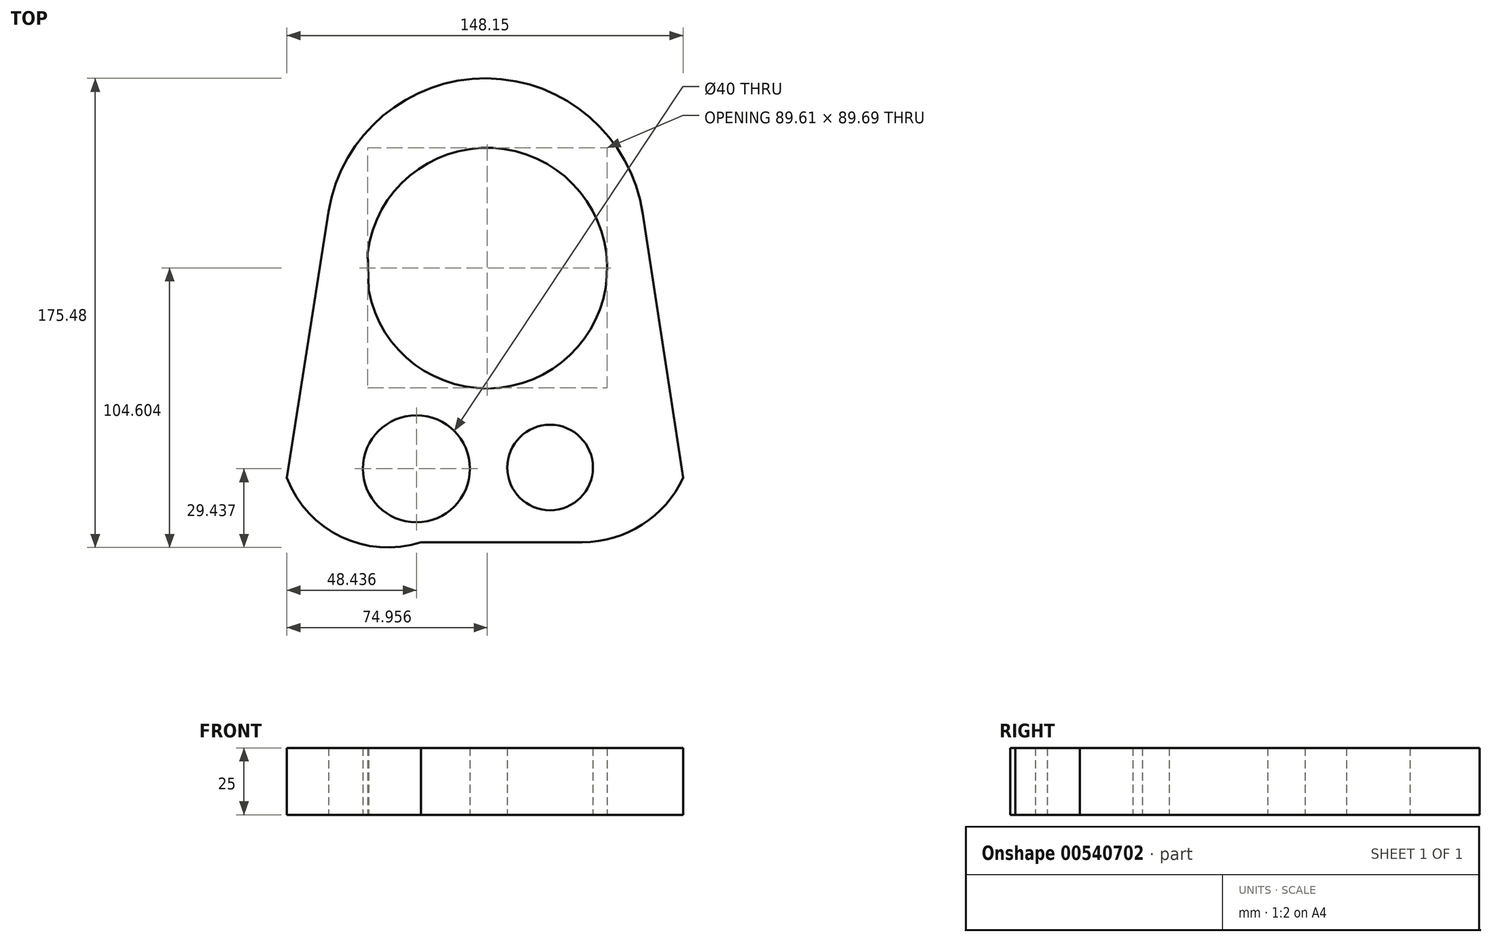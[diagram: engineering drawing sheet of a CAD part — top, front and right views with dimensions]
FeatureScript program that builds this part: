
annotation { "Feature Type Name" : "Feature", "Feature Type Description" : "" }
export const myFeature = defineFeature(function(context is Context, id is Id, definition is map)
    precondition{}
    {
        {
            var Q0;
            Q0=qCreatedBy(makeId("Top.planeOp"),FACE);
            var sketch = newSketch(context, id + "F0", { "sketchPlane" : qUnion([Q0])});
            skCircle(sketch, "E0", {"center": v(-26.34, -32.3) * mm, "radius": 20 * mm});
            skCircle(sketch, "E1", {"center": v(-26.34, -32.3) * mm, "radius": 10 * mm});
            skCircle(sketch, "E2", {"center": v(23.65, -31.82) * mm, "radius": 16 * mm});
            skCircle(sketch, "E3", {"center": v(0, 42.77) * mm, "radius": 16 * mm});
            skArc(sketch, "E4", {"start": v(-44.23, 34.5) * mm, "mid": v(44.98, 44.04) * mm, "end": v(-44.63, 48.53) * mm});
            skLineSegment(sketch, "E5", {"start": v(-44.23, 34.5) * mm, "end": v(-44.63, 48.53) * mm});
            skLineSegment(sketch, "E6", {"start": v(35.7, -59.77) * mm, "end": v(-24.64, -59.77) * mm});
            skArc(sketch, "E7", {"start": v(-74.78, -35.7) * mm, "mid": v(-54.53, -57.75) * mm, "end": v(-24.64, -59.77) * mm});
            skArc(sketch, "E8", {"start": v(35.7, -59.77) * mm, "mid": v(58.05, -53.24) * mm, "end": v(73.37, -35.7) * mm});
            skLineSegment(sketch, "E9", {"start": v(-74.78, -35.7) * mm, "end": v(-59.2, 64.02) * mm});
            skLineSegment(sketch, "E10", {"start": v(73.37, -35.7) * mm, "end": v(58.35, 63.17) * mm});
            skArc(sketch, "E11", {"start": v(58.35, 63.17) * mm, "mid": v(-0.06, 113.75) * mm, "end": v(-59.2, 64.02) * mm});
            skSolve(sketch);
        }
        {
            var Q0;
            Q0 = qSketchRegion(id + "F0", true);
            extrude(context, id + "F1", {"entities" : qUnion([Q0]), "depth" : 25 * mm, "offsetDistance" : 25 * mm});
        }
    });
